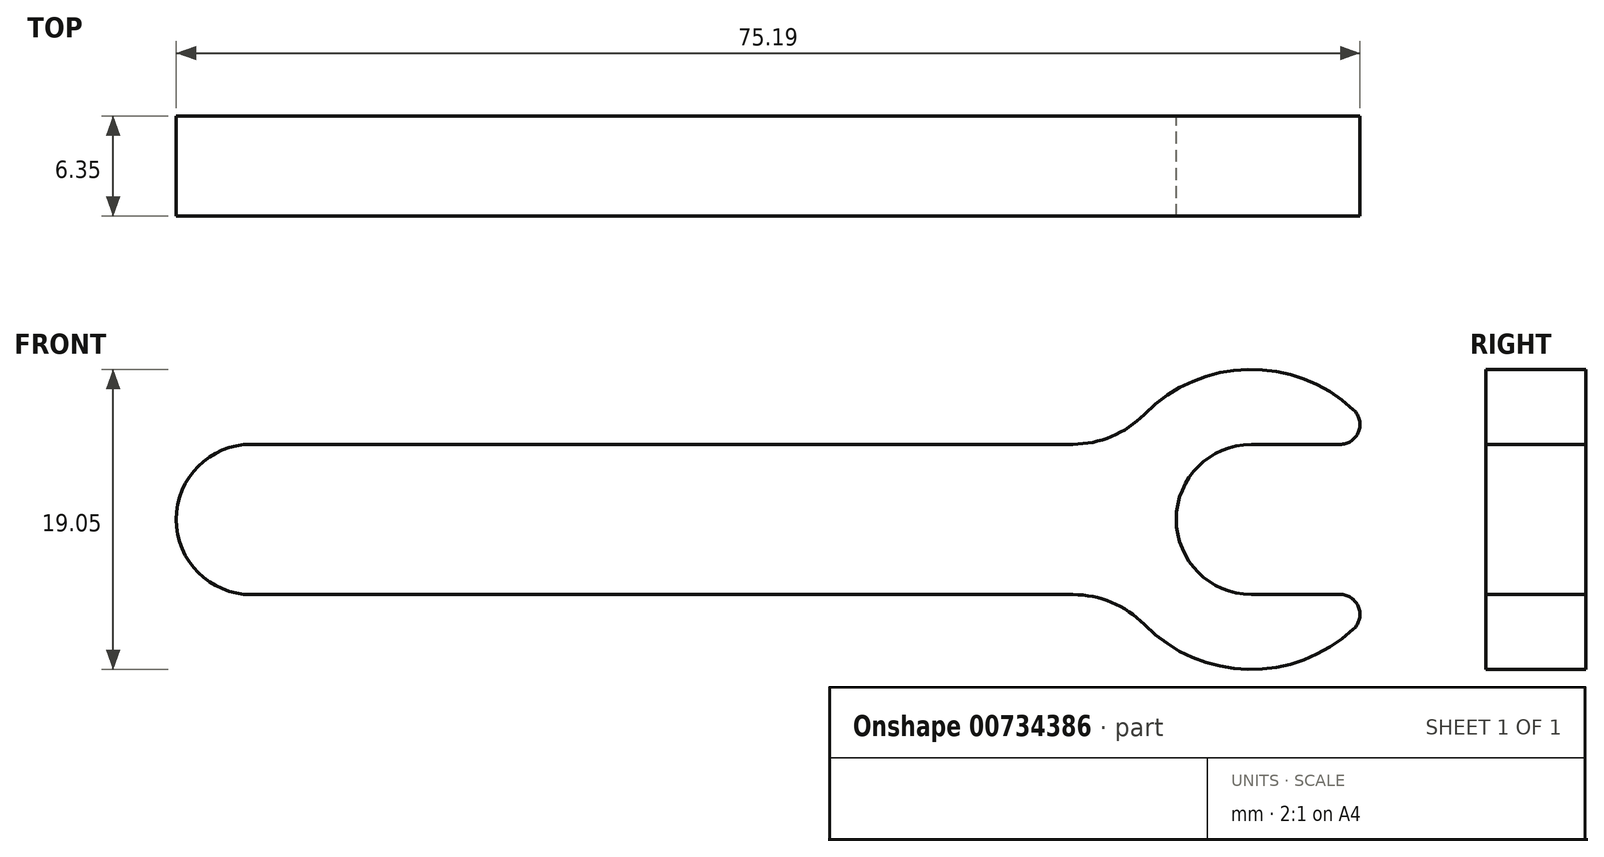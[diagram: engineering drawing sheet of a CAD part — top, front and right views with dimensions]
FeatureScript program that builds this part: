
annotation { "Feature Type Name" : "Feature", "Feature Type Description" : "" }
export const myFeature = defineFeature(function(context is Context, id is Id, definition is map)
    precondition{}
    {
        {
            var Q0;
            Q0=qCreatedBy(makeId("Front.planeOp"),FACE);
            var sketch = newSketch(context, id + "F0", { "sketchPlane" : qUnion([Q0])});
            skLineSegment(sketch, "E0", {"start": v(0, 0) * mm, "end": v(63.5, 0) * mm, "construction": true});
            skLineSegment(sketch, "E1", {"start": v(0, 4.78) * mm, "end": v(52.18, 4.78) * mm});
            skLineSegment(sketch, "E2", {"start": v(0, -4.78) * mm, "end": v(52.18, -4.78) * mm});
            skArc(sketch, "E3", {"start": v(0, 4.78) * mm, "mid": v(-4.78, 0) * mm, "end": v(0, -4.78) * mm});
            skLineSegment(sketch, "E4", {"start": v(69.14, 4.76) * mm, "end": v(63.5, 4.76) * mm});
            skLineSegment(sketch, "E5", {"start": v(69.14, -4.76) * mm, "end": v(63.5, -4.76) * mm});
            skArc(sketch, "E6", {"start": v(63.5, 4.76) * mm, "mid": v(58.74, 0) * mm, "end": v(63.5, -4.76) * mm});
            skArc(sketch, "E7", {"start": v(56.7, -6.68) * mm, "mid": v(54.63, -5.27) * mm, "end": v(52.18, -4.78) * mm});
            skArc(sketch, "E8", {"start": v(52.18, 4.78) * mm, "mid": v(54.63, 5.27) * mm, "end": v(56.7, 6.68) * mm});
            skArc(sketch, "E9", {"start": v(70, 6.96) * mm, "mid": v(63.3, 9.52) * mm, "end": v(56.7, 6.68) * mm});
            skArc(sketch, "E10", {"start": v(69.14, 4.76) * mm, "mid": v(70.32, 5.57) * mm, "end": v(70, 6.96) * mm});
            skArc(sketch, "E11", {"start": v(56.7, -6.68) * mm, "mid": v(63.3, -9.52) * mm, "end": v(70, -6.96) * mm});
            skArc(sketch, "E12", {"start": v(70, -6.96) * mm, "mid": v(70.32, -5.57) * mm, "end": v(69.14, -4.76) * mm});
            skLineSegment(sketch, "E13", {"start": v(63.5, -4.76) * mm, "end": v(63.5, 4.76) * mm, "construction": true});
            skSolve(sketch);
        }
        {
            var Q0;
            Q0 = qSketchRegion(id + "F0", true);
            extrude(context, id + "F1", {"entities" : qUnion([Q0]), "depth" : 6.35 * mm, "offsetDistance" : 25.4 * mm});
        }
    });
